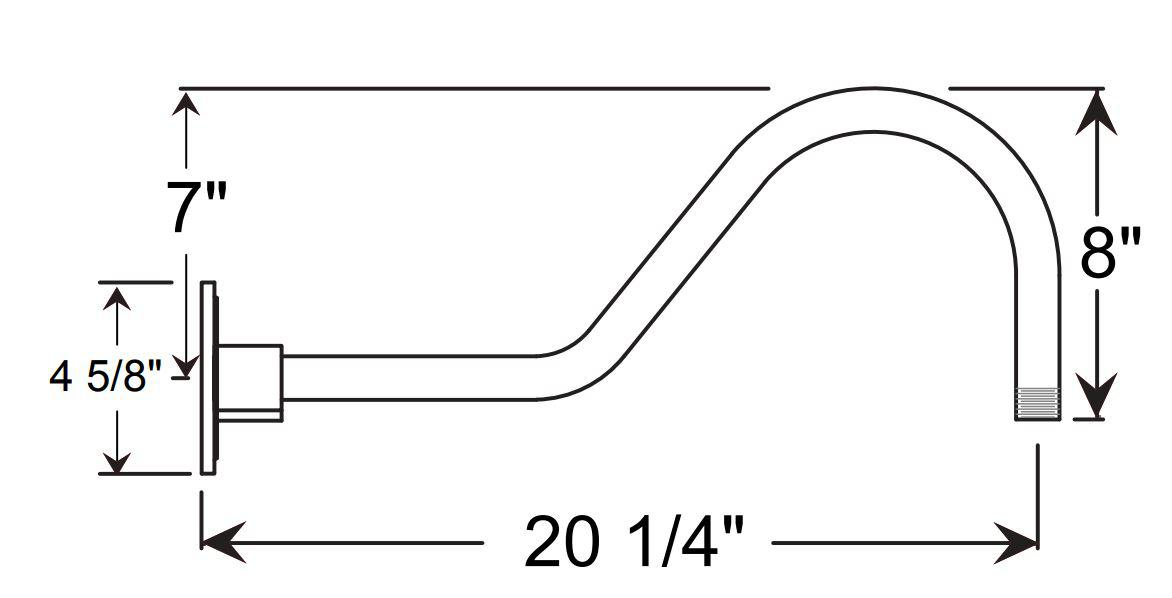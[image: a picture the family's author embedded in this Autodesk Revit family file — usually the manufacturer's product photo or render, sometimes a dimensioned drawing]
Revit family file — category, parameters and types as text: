
# Revit family: Contempo Barn WDU5_14,16,18,20,22
name_source: partatom
category: Lighting Fixtures
units: mm (PartAtom-declared; Revit-internal decimal feet)

## family parameters
Always vertical = Yes
Cut with Voids When Loaded = No
Light Source = Yes
OmniClass Number = 23.80.70.00
OmniClass Title = Lighting
Part Type = Normal
Room Calculation Point = No
Round Connector Dimension = Use Diameter
Shared = No
Work Plane-Based = No

## types (5) — shared parameters
Apparent Load = 200 VA
BULB = Yes
Body Colour = Spun aluminium
Body Material = body
CRI = >90
Canopy Body = Aqua Green
Color Filter = 16777215
Construction Material = Heavy Duty spun aluminum.
Default Elevation = 0' - 0"
Description = 120-277 Voltage
Dimming = 1%
Dimming Lamp Color Temperature Shift = <None>
Efficiency = 65-125 lumens per watt
HUB = Putty
Lamp = Incandescent
Life = L70 50,000 hours
Load Classification = Lighting
Manufacturer = ANP Lighting
Photometric Web File = generic
Power Factor = 1
Tilt Angle = 90.00°
URL = https://www.anplighting.com
Voltage = 120 V
Warranty = 5 year limited warranty
Wattage Comments = 200w Max
b = 0' - 2"

## per-type parameters (varying)
| type | Fixture Diameter | Fixture Height | WDU514 | WDU516 | WDU518 | WDU520 | WDU522 | Weight | a |
| WDU514 | 1' - 2" | 0' - 10 3/4" | Yes | No | No | No | No | 3.7 lb | 0' - 10" |
| WDU516 | 1' - 4" | 0' - 11 1/2" | No | Yes | No | No | No | 4.2 lb | 1' - 0" |
| WDU518 | 1' - 6" | 1' - 0 1/2" | No | No | Yes | No | No | 4.7 lb | 1' - 0" |
| WDU520 | 1' - 8" | 1' - 1 1/4" | No | No | No | Yes | No | 5.2 lb | 1' - 1" |
| WDU522 | 1' - 10" | 1' - 2" | No | No | No | No | Yes | 6.2 lb | 1' - 1" |

note: column(s) folded — value = type name in every type: Model

## geometry (parser evidence)
native form markers: Sweep x39
no freeform markers — native parametric forms only
